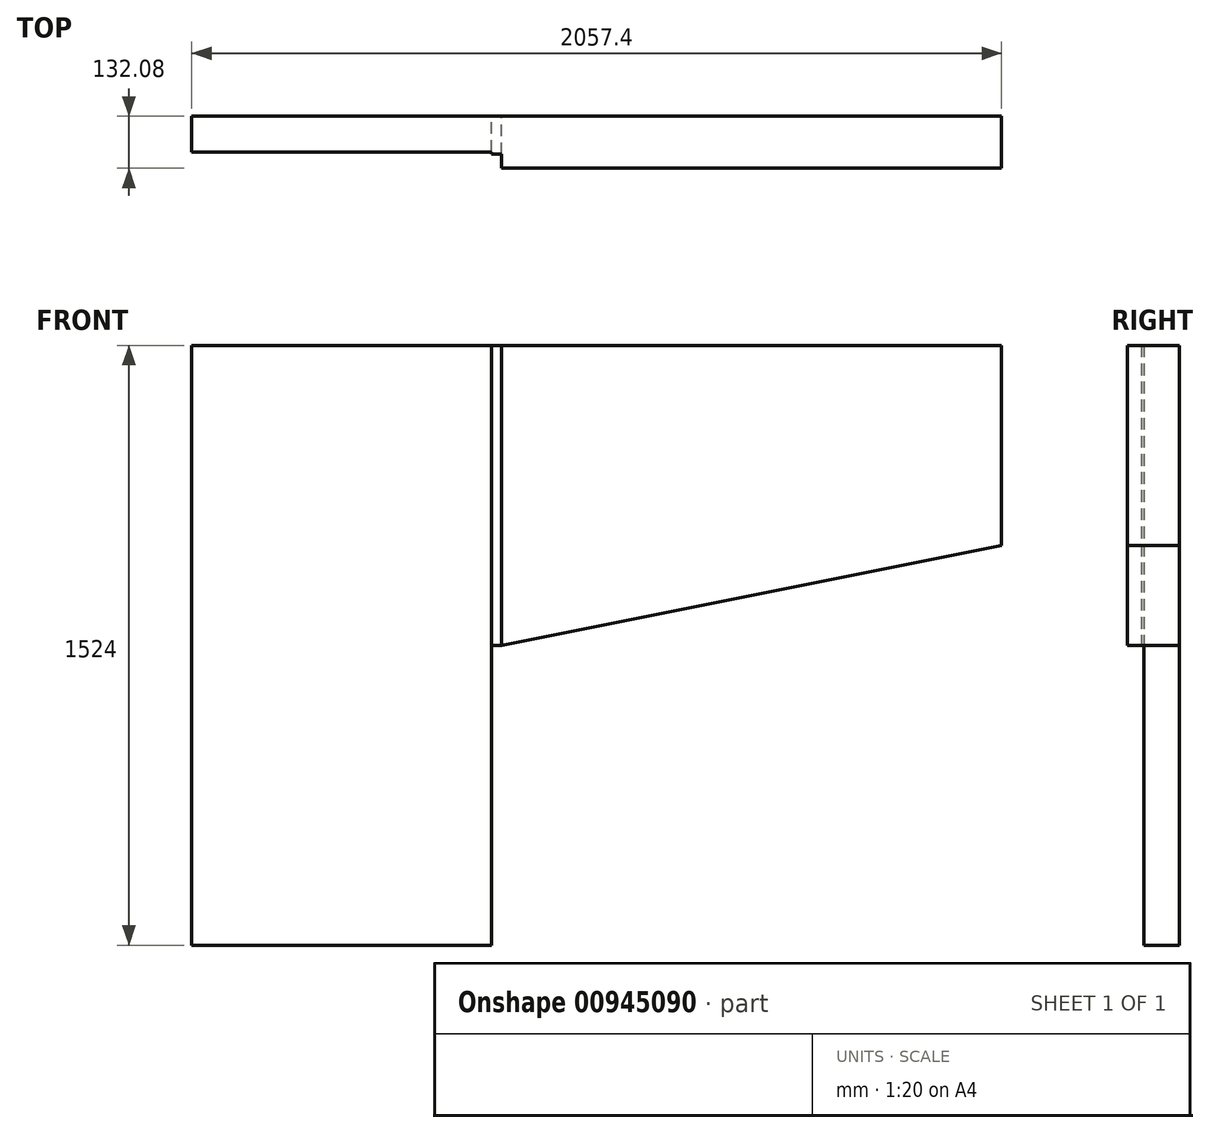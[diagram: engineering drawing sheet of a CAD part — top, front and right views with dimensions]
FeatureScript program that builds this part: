
annotation { "Feature Type Name" : "Feature", "Feature Type Description" : "" }
export const myFeature = defineFeature(function(context is Context, id is Id, definition is map)
    precondition{}
    {
        {
            var Q0;
            Q0=qCreatedBy(makeId("Front.planeOp"),FACE);
            var sketch = newSketch(context, id + "F0", { "sketchPlane" : qUnion([Q0])});
            skLineSegment(sketch, "E0.bottom", {"start": v(-381, 762) * mm, "end": v(381, 762) * mm});
            skLineSegment(sketch, "E0.top", {"start": v(-381, -762) * mm, "end": v(381, -762) * mm});
            skLineSegment(sketch, "E0.left", {"start": v(-381, 762) * mm, "end": v(-381, -762) * mm});
            skLineSegment(sketch, "E0.right", {"start": v(381, 762) * mm, "end": v(381, -762) * mm});
            skPoint(sketch, "E0.middle", {"position": v(0, 0) * mm});
            skSolve(sketch);
        }
        {
            var Q0;
            Q0=qCreatedBy(makeId("Front.planeOp"),FACE);
            var sketch = newSketch(context, id + "F1", { "sketchPlane" : qUnion([Q0])});
            skLineSegment(sketch, "E1.bottom", {"start": v(381, 762) * mm, "end": v(406.4, 762) * mm});
            skLineSegment(sketch, "E1.top", {"start": v(381, 0) * mm, "end": v(406.4, 0) * mm});
            skLineSegment(sketch, "E1.left", {"start": v(381, 762) * mm, "end": v(381, 0) * mm});
            skLineSegment(sketch, "E1.right", {"start": v(406.4, 762) * mm, "end": v(406.4, 0) * mm});
            skSolve(sketch);
        }
        {
            var Q0;
            Q0=qCreatedBy(makeId("Front.planeOp"),FACE);
            var sketch = newSketch(context, id + "F2", { "sketchPlane" : qUnion([Q0])});
            skLineSegment(sketch, "E2", {"start": v(406.4, 762) * mm, "end": v(1676.4, 762) * mm});
            skLineSegment(sketch, "E3", {"start": v(1676.4, 762) * mm, "end": v(1676.4, 254) * mm});
            skLineSegment(sketch, "E4", {"start": v(406.4, 0) * mm, "end": v(1676.4, 254) * mm});
            skLineSegment(sketch, "E5", {"start": v(406.4, 0) * mm, "end": v(406.4, 762) * mm});
            skSolve(sketch);
        }
        {
            var Q0;
            Q0=qSketchRegion(id+"F0",true);
            extrude(context, id + "F3", {"entities" : qUnion([Q0]), "depth" : 90.42 * mm, "offsetDistance" : 25.4 * mm});
        }
        {
            var Q0;
            Q0=qSketchRegion(id+"F1",true);
            extrude(context, id + "F4", {"entities" : qUnion([Q0]), "operationType" : NewBodyOperationType.ADD, "depth" : 96.52 * mm, "offsetDistance" : 25.4 * mm});
        }
        {
            var Q0;
            Q0=qSketchRegion(id+"F2",true);
            extrude(context, id + "F5", {"entities" : qUnion([Q0]), "operationType" : NewBodyOperationType.ADD, "depth" : 132.08 * mm, "offsetDistance" : 25.4 * mm});
        }
    });
